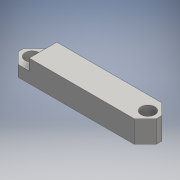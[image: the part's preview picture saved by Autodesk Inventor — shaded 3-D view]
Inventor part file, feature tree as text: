
AUTODESK INVENTOR PART (.ipt)
format: ipt  version: 2016 (Build 200138000, 138)  size: 126,976 bytes
history: native  units: mm
features: extrude x4, chamfer x4, sketch x4, other x1
ambient origin geometry x8: Origin, YZ Plane, XZ Plane, XY Plane, X Axis, Y Axis, Z Axis, Center Point
bodies: Body1 (feature_tree)
feature tree (13):
  other  "ソリッド1"
  extrude  "押し出し1"  Depth=25.0mm
  extrude  "押し出し2"  Depth=4.0mm
  chamfer  "面取り1"  Distance=5.0mm
  chamfer  "面取り2"  Distance=2.5mm
  extrude  "押し出し3"  Depth=2.0mm
  chamfer  "面取り3"  Distance=5.0mm
  chamfer  "面取り4"  Distance=2.0mm Angle=45.0deg
  extrude  "押し出し4"  Depth=2.0mm TaperAngle=45.0deg
  sketch  "スケッチ1"
  sketch  "スケッチ2"
  sketch  "スケッチ3"
  sketch  "スケッチ4"
